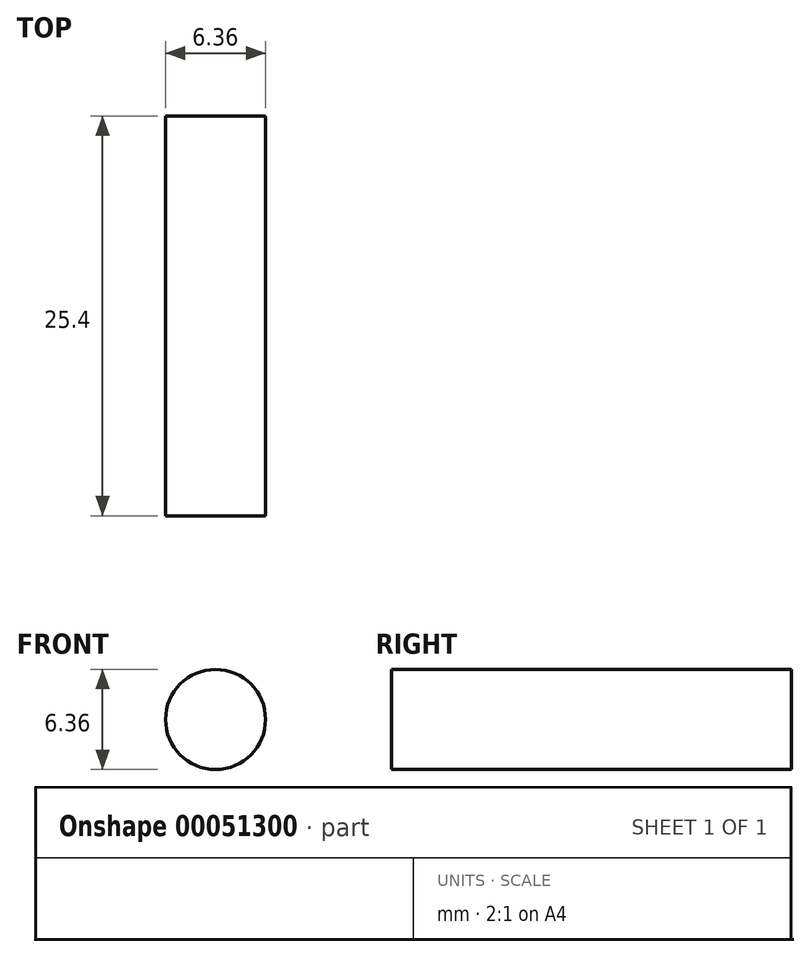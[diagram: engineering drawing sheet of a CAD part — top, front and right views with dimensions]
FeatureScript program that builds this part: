
annotation { "Feature Type Name" : "Feature", "Feature Type Description" : "" }
export const myFeature = defineFeature(function(context is Context, id is Id, definition is map)
    precondition{}
    {
        {
            var Q0;
            Q0=qCreatedBy(makeId("Front.planeOp"),FACE);
            var sketch = newSketch(context, id + "F0", { "sketchPlane" : qUnion([Q0])});
            skCircle(sketch, "E0", {"center": v(0, 0) * mm, "radius": 3.18 * mm});
            skSolve(sketch);
        }
        {
            var Q0;
            Q0=makeQuery(id+"F0.imprint","IMPRINT",FACE,{"disambiguationData":[TD([[makeQuery(id+"F0.imprint","IMPRINT",EDGE,{"derivedFrom":sQuery(id+"F0.wireOp",EDGE,"E0")}),1.0]])]});
            extrude(context, id + "F1", {"entities" : qUnion([Q0]), "depth" : 25.4 * mm});
        }
    });
